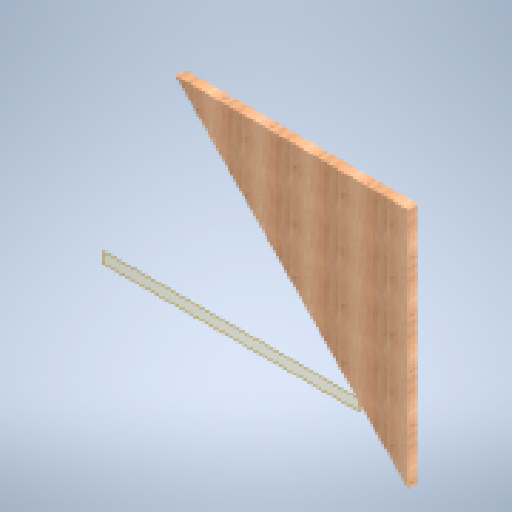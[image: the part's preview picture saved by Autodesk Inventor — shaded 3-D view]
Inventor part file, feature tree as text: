
AUTODESK INVENTOR PART (.ipt)
format: ipt  version: 2025 (Build 290162000, 162)  size: 149,504 bytes
history: native  units: in
note: dims shown in document units (in); Inventor stores cm internally (conversion verified against a paired STEP export)
features: other x3, sketch x1, plane x1
ambient origin geometry x8: Origin, YZ Plane, XZ Plane, XY Plane, X Axis, Y Axis, Z Axis, Center Point
bodies: Solid1 (feature_tree)
feature tree (5):
  other  "leg slant.ipt"
  other  "Solid3::leg slant.ipt"
  other  "TaggingFeature1"
  sketch  "Sketch1"  dims[d0=0.3937in]
  plane  "Work Plane1"
